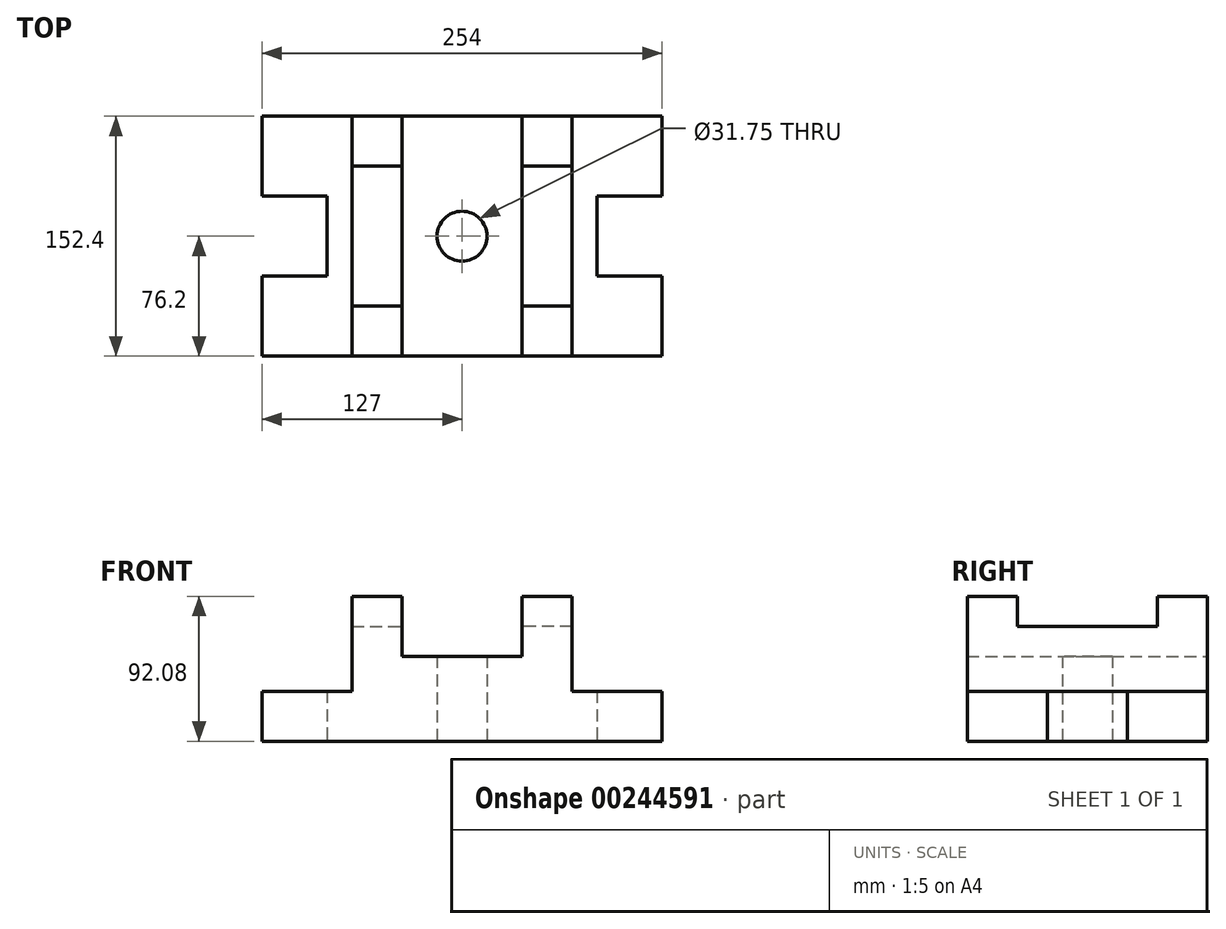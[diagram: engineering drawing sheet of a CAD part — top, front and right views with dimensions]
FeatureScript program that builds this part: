
annotation { "Feature Type Name" : "Feature", "Feature Type Description" : "" }
export const myFeature = defineFeature(function(context is Context, id is Id, definition is map)
    precondition{}
    {
        {
            var Q0;
            Q0=qCreatedBy(makeId("Top.planeOp"),FACE);
            var sketch = newSketch(context, id + "F0", { "sketchPlane" : qUnion([Q0])});
            skCircle(sketch, "E0", {"center": v(0, 0) * mm, "radius": 15.88 * mm});
            skLineSegment(sketch, "E1", {"start": v(-127, -76.2) * mm, "end": v(127, -76.2) * mm});
            skLineSegment(sketch, "E2", {"start": v(-127, -76.2) * mm, "end": v(-127, -25.4) * mm});
            skLineSegment(sketch, "E3", {"start": v(-127, -25.4) * mm, "end": v(-85.73, -25.4) * mm});
            skLineSegment(sketch, "E4", {"start": v(-85.73, -25.4) * mm, "end": v(-85.73, 25.4) * mm});
            skLineSegment(sketch, "E5", {"start": v(-127, 25.4) * mm, "end": v(-85.73, 25.4) * mm});
            skLineSegment(sketch, "E6", {"start": v(-127, 25.4) * mm, "end": v(-127, 76.2) * mm});
            skLineSegment(sketch, "E7", {"start": v(-127, 76.2) * mm, "end": v(127, 76.2) * mm});
            skLineSegment(sketch, "E8", {"start": v(127, 76.2) * mm, "end": v(127, 25.4) * mm});
            skLineSegment(sketch, "E9", {"start": v(127, -76.2) * mm, "end": v(127, -25.4) * mm});
            skLineSegment(sketch, "E10", {"start": v(127, 25.4) * mm, "end": v(85.73, 25.4) * mm});
            skLineSegment(sketch, "E11", {"start": v(127, -25.4) * mm, "end": v(85.72, -25.4) * mm});
            skLineSegment(sketch, "E12", {"start": v(85.73, 25.4) * mm, "end": v(85.72, -25.4) * mm});
            skLineSegment(sketch, "E13", {"start": v(69.85, 76.2) * mm, "end": v(69.85, -76.2) * mm});
            skLineSegment(sketch, "E14", {"start": v(38.1, 76.2) * mm, "end": v(38.1, 44.45) * mm});
            skLineSegment(sketch, "E15", {"start": v(38.1, 44.45) * mm, "end": v(69.85, 44.45) * mm});
            skLineSegment(sketch, "E16", {"start": v(38.1, -76.2) * mm, "end": v(38.1, -44.45) * mm});
            skLineSegment(sketch, "E17", {"start": v(38.1, -44.45) * mm, "end": v(69.85, -44.45) * mm});
            skLineSegment(sketch, "E18", {"start": v(38.1, 44.45) * mm, "end": v(38.1, -44.45) * mm});
            skLineSegment(sketch, "E19", {"start": v(-38.1, 76.2) * mm, "end": v(-38.1, 44.45) * mm});
            skLineSegment(sketch, "E20", {"start": v(-38.1, 44.45) * mm, "end": v(-69.85, 44.45) * mm});
            skLineSegment(sketch, "E21", {"start": v(-69.85, 44.45) * mm, "end": v(-69.85, 76.2) * mm});
            skLineSegment(sketch, "E22", {"start": v(-69.85, 44.45) * mm, "end": v(-69.85, -76.2) * mm});
            skLineSegment(sketch, "E23", {"start": v(-69.85, -76.2) * mm, "end": v(-69.85, 44.45) * mm});
            skLineSegment(sketch, "E24", {"start": v(-38.1, 44.45) * mm, "end": v(-38.1, -76.2) * mm});
            skLineSegment(sketch, "E25", {"start": v(-38.1, -44.45) * mm, "end": v(-69.85, -44.45) * mm});
            skSolve(sketch);
        }
        {
            var Q0;
            Q0 = qSketchRegion(id + "F0", true);
            var Q1;
            {var subQ0=sQuery(id+"F0.wireOp",EDGE,"E20");Q1=makeQuery(id+"F0.imprint","IMPRINT",FACE,{"disambiguationData":[TD([[makeQuery(id+"F0.imprint","IMPRINT",EDGE,{"derivedFrom":subQ0}),1.0]])]});}
            var Q2;
            {var subQ0=sQuery(id+"F0.wireOp",EDGE,"E15");Q2=makeQuery(id+"F0.imprint","IMPRINT",FACE,{"disambiguationData":[TD([[makeQuery(id+"F0.imprint","IMPRINT",EDGE,{"derivedFrom":subQ0}),-1.0]])]});}
            extrude(context, id + "F1", {"entities" : qUnion([Q0, Q1, Q2]), "depth" : 31.75 * mm});
        }
        {
            var Q0;
            {var subQ5=sQuery(id+"F0.wireOp",EDGE,"E25");Q0=makeQuery(id+"F0.imprint","IMPRINT",FACE,{"disambiguationData":[TD([[makeQuery(id+"F0.imprint","IMPRINT",EDGE,{"derivedFrom":subQ5}),1.0]])]});}
            var Q1;
            {var subQ0=sQuery(id+"F0.wireOp",EDGE,"E20");Q1=makeQuery(id+"F0.imprint","IMPRINT",FACE,{"disambiguationData":[TD([[makeQuery(id+"F0.imprint","IMPRINT",EDGE,{"derivedFrom":subQ0}),1.0]])]});}
            var Q2;
            {var subQ0=sQuery(id+"F0.wireOp",EDGE,"E19");Q2=makeQuery(id+"F0.imprint","IMPRINT",FACE,{"disambiguationData":[TD([[makeQuery(id+"F0.imprint","IMPRINT",EDGE,{"derivedFrom":subQ0}),-1.0]])]});}
            var Q3;
            Q3=makeQuery(id+"F0.imprint","IMPRINT",FACE,{"disambiguationData":[TD([[makeQuery(id+"F0.imprint","IMPRINT",EDGE,{"derivedFrom":sQuery(id+"F0.wireOp",EDGE,"E0")}),-1.0]])]});
            var Q4;
            {var subQ3=sQuery(id+"F0.wireOp",EDGE,"E14");Q4=makeQuery(id+"F0.imprint","IMPRINT",FACE,{"disambiguationData":[TD([[makeQuery(id+"F0.imprint","IMPRINT",EDGE,{"derivedFrom":subQ3}),1.0]])]});}
            var Q5;
            {var subQ0=sQuery(id+"F0.wireOp",EDGE,"E15");Q5=makeQuery(id+"F0.imprint","IMPRINT",FACE,{"disambiguationData":[TD([[makeQuery(id+"F0.imprint","IMPRINT",EDGE,{"derivedFrom":subQ0}),-1.0]])]});}
            var Q6;
            {var subQ3=sQuery(id+"F0.wireOp",EDGE,"E16");Q6=makeQuery(id+"F0.imprint","IMPRINT",FACE,{"disambiguationData":[TD([[makeQuery(id+"F0.imprint","IMPRINT",EDGE,{"derivedFrom":subQ3}),-1.0]])]});}
            extrude(context, id + "F2", {"entities" : qUnion([Q0, Q1, Q2, Q3, Q4, Q5, Q6]), "operationType" : NewBodyOperationType.ADD, "depth" : 53.97 * mm});
        }
        {
            var Q0;
            {var subQ0=sQuery(id+"F0.wireOp",EDGE,"E20");Q0=makeQuery(id+"F0.imprint","IMPRINT",FACE,{"disambiguationData":[TD([[makeQuery(id+"F0.imprint","IMPRINT",EDGE,{"derivedFrom":subQ0}),1.0]])]});}
            var Q1;
            {var subQ5=sQuery(id+"F0.wireOp",EDGE,"E25");Q1=makeQuery(id+"F0.imprint","IMPRINT",FACE,{"disambiguationData":[TD([[makeQuery(id+"F0.imprint","IMPRINT",EDGE,{"derivedFrom":subQ5}),1.0]])]});}
            var Q2;
            {var subQ0=sQuery(id+"F0.wireOp",EDGE,"E19");Q2=makeQuery(id+"F0.imprint","IMPRINT",FACE,{"disambiguationData":[TD([[makeQuery(id+"F0.imprint","IMPRINT",EDGE,{"derivedFrom":subQ0}),-1.0]])]});}
            var Q3;
            {var subQ3=sQuery(id+"F0.wireOp",EDGE,"E14");Q3=makeQuery(id+"F0.imprint","IMPRINT",FACE,{"disambiguationData":[TD([[makeQuery(id+"F0.imprint","IMPRINT",EDGE,{"derivedFrom":subQ3}),1.0]])]});}
            var Q4;
            {var subQ0=sQuery(id+"F0.wireOp",EDGE,"E15");Q4=makeQuery(id+"F0.imprint","IMPRINT",FACE,{"disambiguationData":[TD([[makeQuery(id+"F0.imprint","IMPRINT",EDGE,{"derivedFrom":subQ0}),-1.0]])]});}
            var Q5;
            {var subQ3=sQuery(id+"F0.wireOp",EDGE,"E16");Q5=makeQuery(id+"F0.imprint","IMPRINT",FACE,{"disambiguationData":[TD([[makeQuery(id+"F0.imprint","IMPRINT",EDGE,{"derivedFrom":subQ3}),-1.0]])]});}
            extrude(context, id + "F3", {"entities" : qUnion([Q0, Q1, Q2, Q3, Q4, Q5]), "operationType" : NewBodyOperationType.ADD, "depth" : 73.02 * mm});
        }
        {
            var Q0;
            {var subQ5=sQuery(id+"F0.wireOp",EDGE,"E25");Q0=makeQuery(id+"F0.imprint","IMPRINT",FACE,{"disambiguationData":[TD([[makeQuery(id+"F0.imprint","IMPRINT",EDGE,{"derivedFrom":subQ5}),1.0]])]});}
            var Q1;
            {var subQ3=sQuery(id+"F0.wireOp",EDGE,"E16");Q1=makeQuery(id+"F0.imprint","IMPRINT",FACE,{"disambiguationData":[TD([[makeQuery(id+"F0.imprint","IMPRINT",EDGE,{"derivedFrom":subQ3}),-1.0]])]});}
            var Q2;
            {var subQ3=sQuery(id+"F0.wireOp",EDGE,"E14");Q2=makeQuery(id+"F0.imprint","IMPRINT",FACE,{"disambiguationData":[TD([[makeQuery(id+"F0.imprint","IMPRINT",EDGE,{"derivedFrom":subQ3}),1.0]])]});}
            var Q3;
            {var subQ0=sQuery(id+"F0.wireOp",EDGE,"E19");Q3=makeQuery(id+"F0.imprint","IMPRINT",FACE,{"disambiguationData":[TD([[makeQuery(id+"F0.imprint","IMPRINT",EDGE,{"derivedFrom":subQ0}),-1.0]])]});}
            extrude(context, id + "F4", {"entities" : qUnion([Q0, Q1, Q2, Q3]), "operationType" : NewBodyOperationType.ADD, "depth" : 92.07 * mm});
        }
    });
